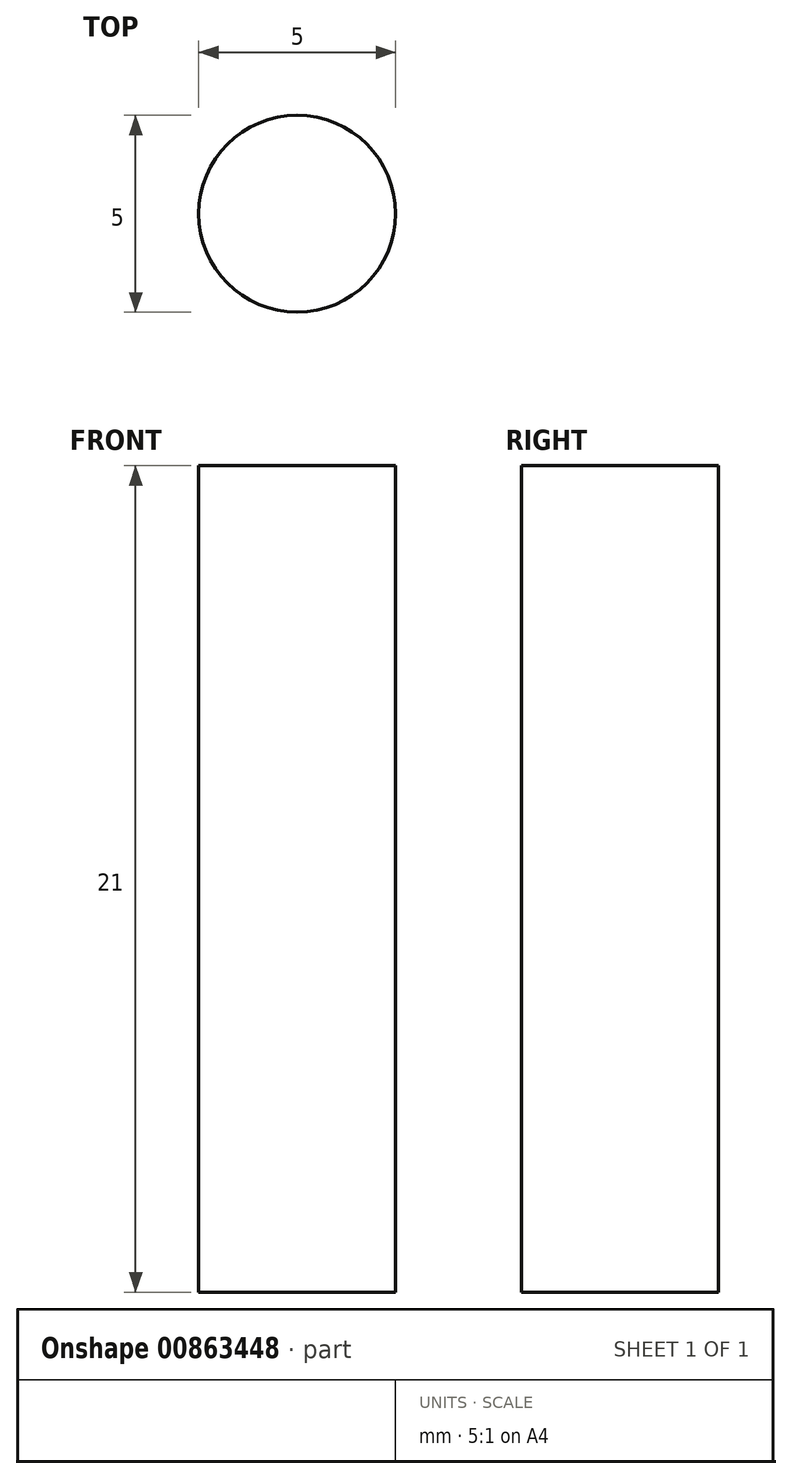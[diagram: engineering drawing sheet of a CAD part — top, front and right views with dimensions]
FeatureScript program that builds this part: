
annotation { "Feature Type Name" : "Feature", "Feature Type Description" : "" }
export const myFeature = defineFeature(function(context is Context, id is Id, definition is map)
    precondition{}
    {
        {
            var Q0;
            Q0=qCreatedBy(makeId("Top.planeOp"),FACE);
            var sketch = newSketch(context, id + "F0", { "sketchPlane" : qUnion([Q0])});
            skCircle(sketch, "E0", {"center": v(0, 0) * mm, "radius": 2.5 * mm});
            skSolve(sketch);
        }
        {
            var Q0;
            Q0=makeQuery(id+"F0.imprint","IMPRINT",FACE,{"disambiguationData":[TD([[makeQuery(id+"F0.imprint","IMPRINT",EDGE,{"derivedFrom":sQuery(id+"F0.wireOp",EDGE,"E0")}),1.0]])]});
            extrude(context, id + "F1", {"entities" : qUnion([Q0]), "depth" : 21 * mm, "offsetDistance" : 25 * mm});
        }
    });
